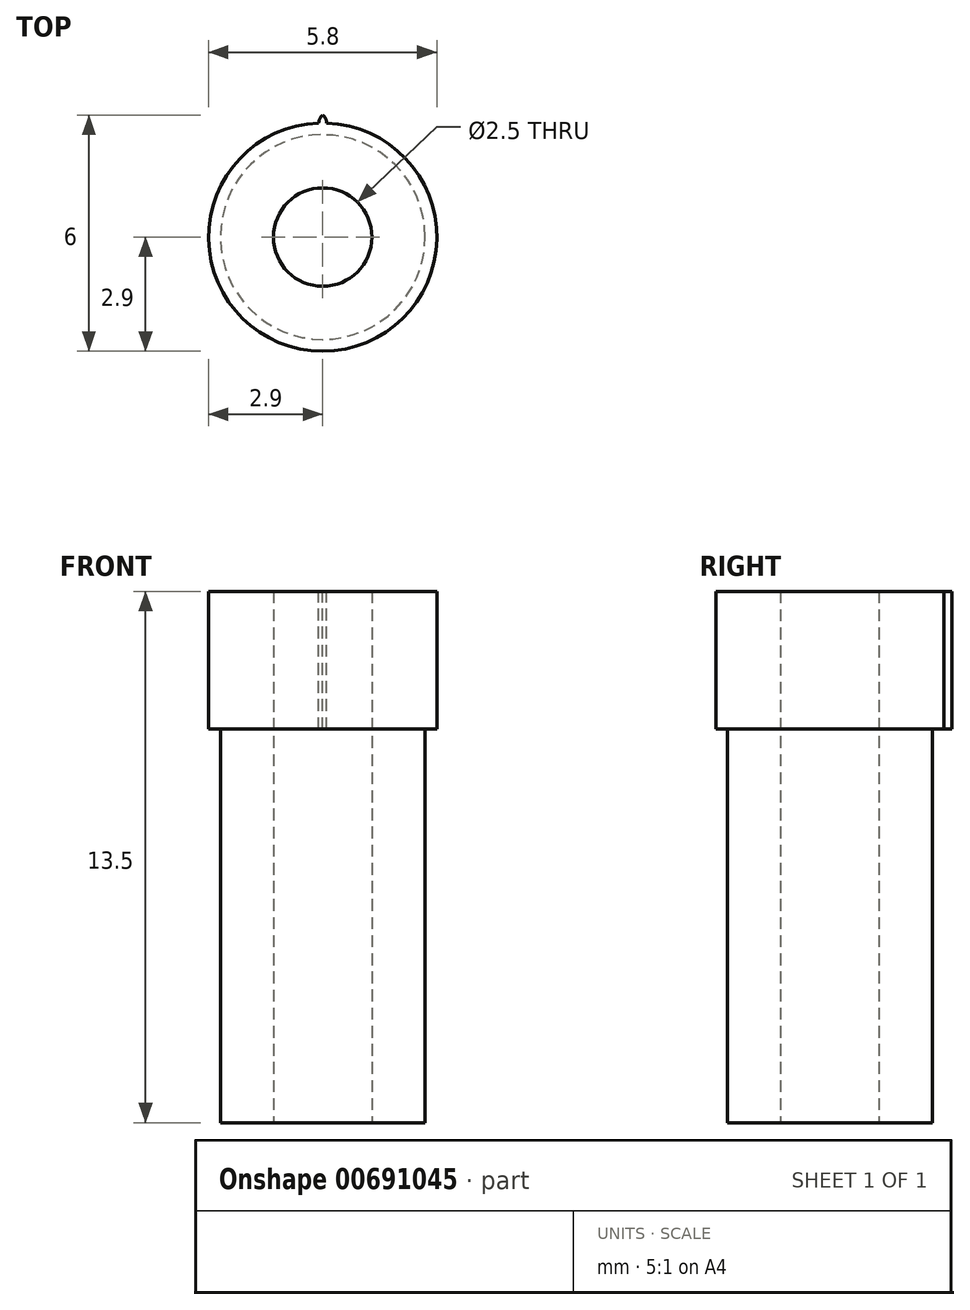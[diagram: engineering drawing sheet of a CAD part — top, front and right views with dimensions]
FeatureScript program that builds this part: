
annotation { "Feature Type Name" : "Feature", "Feature Type Description" : "" }
export const myFeature = defineFeature(function(context is Context, id is Id, definition is map)
    precondition{}
    {
        {
            var Q0;
            Q0=qCreatedBy(makeId("Front.planeOp"),FACE);
            var sketch = newSketch(context, id + "F0", { "sketchPlane" : qUnion([Q0])});
            skLineSegment(sketch, "E0", {"start": v(0, -1.67) * mm, "end": v(0, 2.45) * mm, "construction": true});
            skLineSegment(sketch, "E1", {"start": v(1.25, 0) * mm, "end": v(1.25, 13.5) * mm});
            skLineSegment(sketch, "E2", {"start": v(1.25, 13.5) * mm, "end": v(2.9, 13.5) * mm});
            skLineSegment(sketch, "E3", {"start": v(2.9, 13.5) * mm, "end": v(2.9, 10) * mm});
            skLineSegment(sketch, "E4", {"start": v(2.9, 10) * mm, "end": v(2.6, 10) * mm});
            skLineSegment(sketch, "E5", {"start": v(2.6, 10) * mm, "end": v(2.6, 0) * mm});
            skLineSegment(sketch, "E6", {"start": v(2.6, 0) * mm, "end": v(1.25, 0) * mm});
            skSolve(sketch);
        }
        {
            var Q0;
            Q0=makeQuery(id+"F0.imprint","IMPRINT",FACE,{"disambiguationData":[TD([[makeQuery(id+"F0.imprint","IMPRINT",EDGE,{"derivedFrom":sQuery(id+"F0.wireOp",EDGE,"E1")}),-1.0]])]});
            var Q1;
            Q1=sQuery(id+"F0.wireOp",EDGE,"E0");
            revolve(context, id + "F1", {"entities" : qUnion([Q0]), "axis" : qUnion([Q1]), "revolveType" : RevolveType.FULL});
        }
        {
            var Q0;
            Q0=makeQuery(id+"F1.opRevolve","SWEPT_FACE",FACE,{"disambiguationData":[OSD([sQuery(id+"F0.wireOp",EDGE,"E2")])]});
            var sketch = newSketch(context, id + "F2", { "sketchPlane" : qUnion([Q0])});
            skArc(sketch, "E7", {"start": v(0.1, 2.9) * mm, "mid": v(0.07, 3.01) * mm, "end": v(0, 3.1) * mm});
            skArc(sketch, "E8", {"start": v(0, 3.1) * mm, "mid": v(-0.07, 3.01) * mm, "end": v(-0.1, 2.9) * mm});
            skLineSegment(sketch, "E9", {"start": v(-0.15, 2.9) * mm, "end": v(0.15, 2.9) * mm, "construction": true});
            skArc(sketch, "E10", {"start": v(0.1, 2.9) * mm, "mid": v(0, 2.9) * mm, "end": v(-0.1, 2.9) * mm});
            skSolve(sketch);
        }
        {
            var Q0;
            Q0=makeQuery(id+"F2.imprint","IMPRINT",FACE,{"disambiguationData":[TD([[makeQuery(id+"F2.imprint","IMPRINT",EDGE,{"derivedFrom":sQuery(id+"F2.wireOp",EDGE,"E7")}),1.0]])]});
            var Q1;
            Q1=makeQuery(id+"F1.opRevolve","SWEPT_FACE",FACE,{"disambiguationData":[OSD([sQuery(id+"F0.wireOp",EDGE,"E4")])]});
            extrude(context, id + "F3", {"entities" : qUnion([Q0]), "operationType" : NewBodyOperationType.ADD, "endBound" : BoundingType.UP_TO_SURFACE, "oppositeDirection" : true, "depth" : 25 * mm, "endBoundEntityFace" : qUnion([Q1]), "offsetDistance" : 25 * mm});
        }
    });
